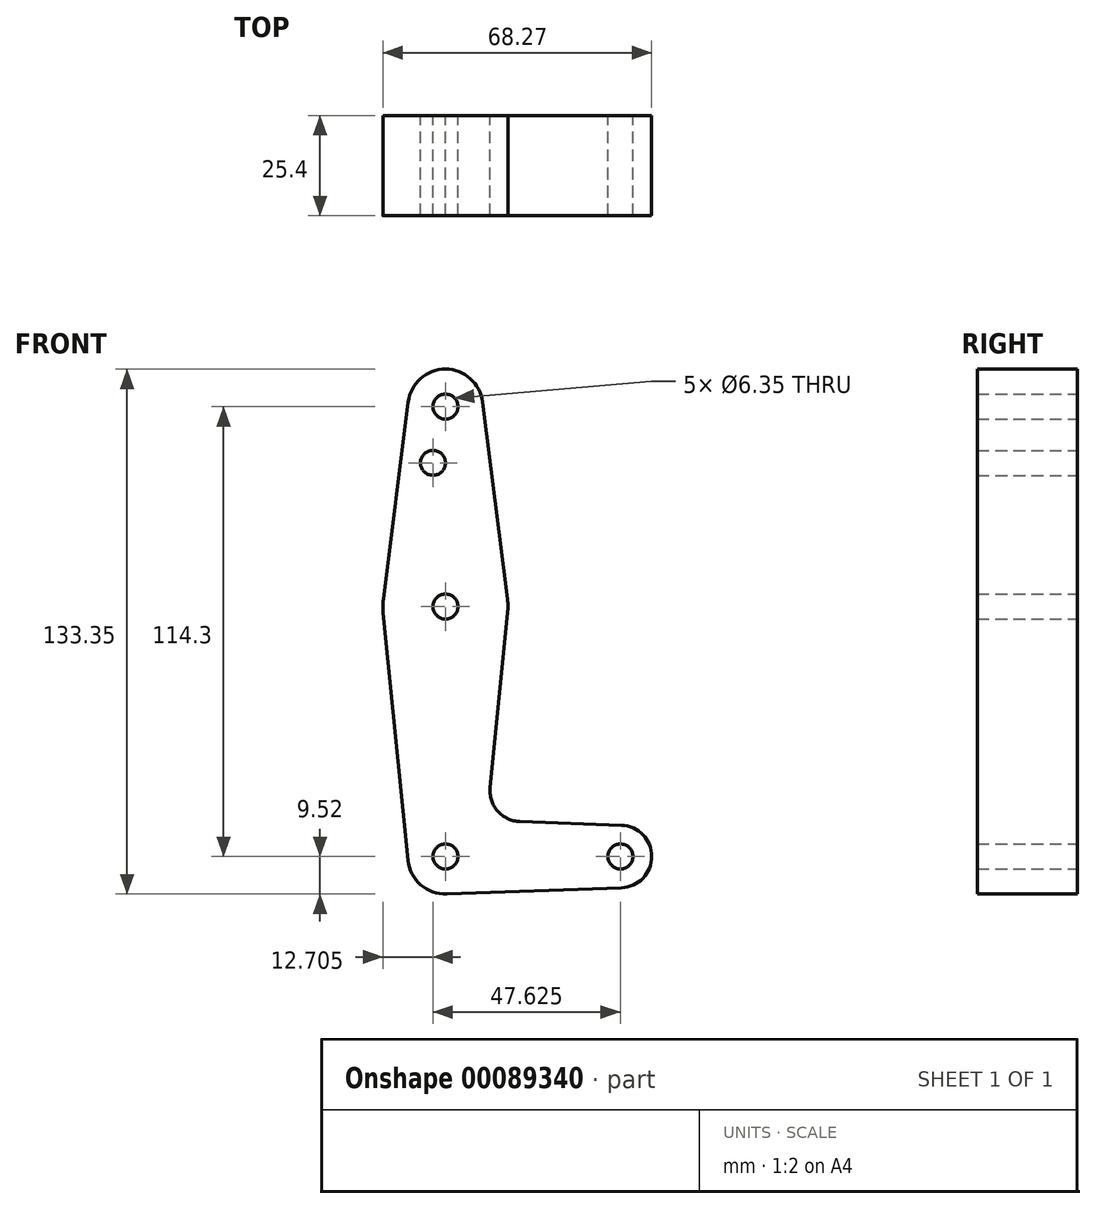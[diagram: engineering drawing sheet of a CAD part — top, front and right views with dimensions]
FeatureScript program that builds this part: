
annotation { "Feature Type Name" : "Feature", "Feature Type Description" : "" }
export const myFeature = defineFeature(function(context is Context, id is Id, definition is map)
    precondition{}
    {
        {
            var Q0;
            Q0=qCreatedBy(makeId("Front.planeOp"),FACE);
            var sketch = newSketch(context, id + "F0", { "sketchPlane" : qUnion([Q0])});
            skCircle(sketch, "E0", {"center": v(0, 114.3) * mm, "radius": 9.53 * mm});
            skCircle(sketch, "E1", {"center": v(0, 0) * mm, "radius": 9.53 * mm});
            skCircle(sketch, "E2", {"center": v(44.45, 0) * mm, "radius": 7.94 * mm});
            skLineSegment(sketch, "E3", {"start": v(9.45, 115.5) * mm, "end": v(15.75, 65.48) * mm});
            skLineSegment(sketch, "E4", {"start": v(-9.45, 115.5) * mm, "end": v(-15.75, 65.48) * mm});
            skLineSegment(sketch, "E5", {"start": v(-15.8, 61.91) * mm, "end": v(-9.48, -0.95) * mm});
            skLineSegment(sketch, "E6", {"start": v(0, -9.53) * mm, "end": v(44.73, -7.93) * mm});
            skCircle(sketch, "E7", {"center": v(0, 114.3) * mm, "radius": 3.18 * mm});
            skCircle(sketch, "E8", {"center": v(0, 63.5) * mm, "radius": 3.18 * mm});
            skCircle(sketch, "E9", {"center": v(0, 0) * mm, "radius": 3.18 * mm});
            skCircle(sketch, "E10", {"center": v(44.45, 0) * mm, "radius": 3.18 * mm});
            skArc(sketch, "E11", {"start": v(11.34, 17.6) * mm, "mid": v(13.26, 11.57) * mm, "end": v(18.97, 8.85) * mm});
            skCircle(sketch, "E12", {"center": v(-3.17, 100.03) * mm, "radius": 3.18 * mm});
            skLineSegment(sketch, "E13", {"start": v(0, 114.3) * mm, "end": v(0, 63.5) * mm});
            skCircle(sketch, "E14", {"center": v(0, 63.5) * mm, "radius": 15.87 * mm});
            skLineSegment(sketch, "E15.trimOffspring", {"start": v(11.34, 17.6) * mm, "end": v(15.8, 61.91) * mm});
            skLineSegment(sketch, "E16.trimOffspring", {"start": v(18.97, 8.85) * mm, "end": v(44.73, 7.93) * mm});
            skSolve(sketch);
        }
        {
            var Q0;
            Q0 = qSketchRegion(id + "F0", true);
            extrude(context, id + "F1", {"entities" : qUnion([Q0]), "depth" : 25.4 * mm});
        }
    });
